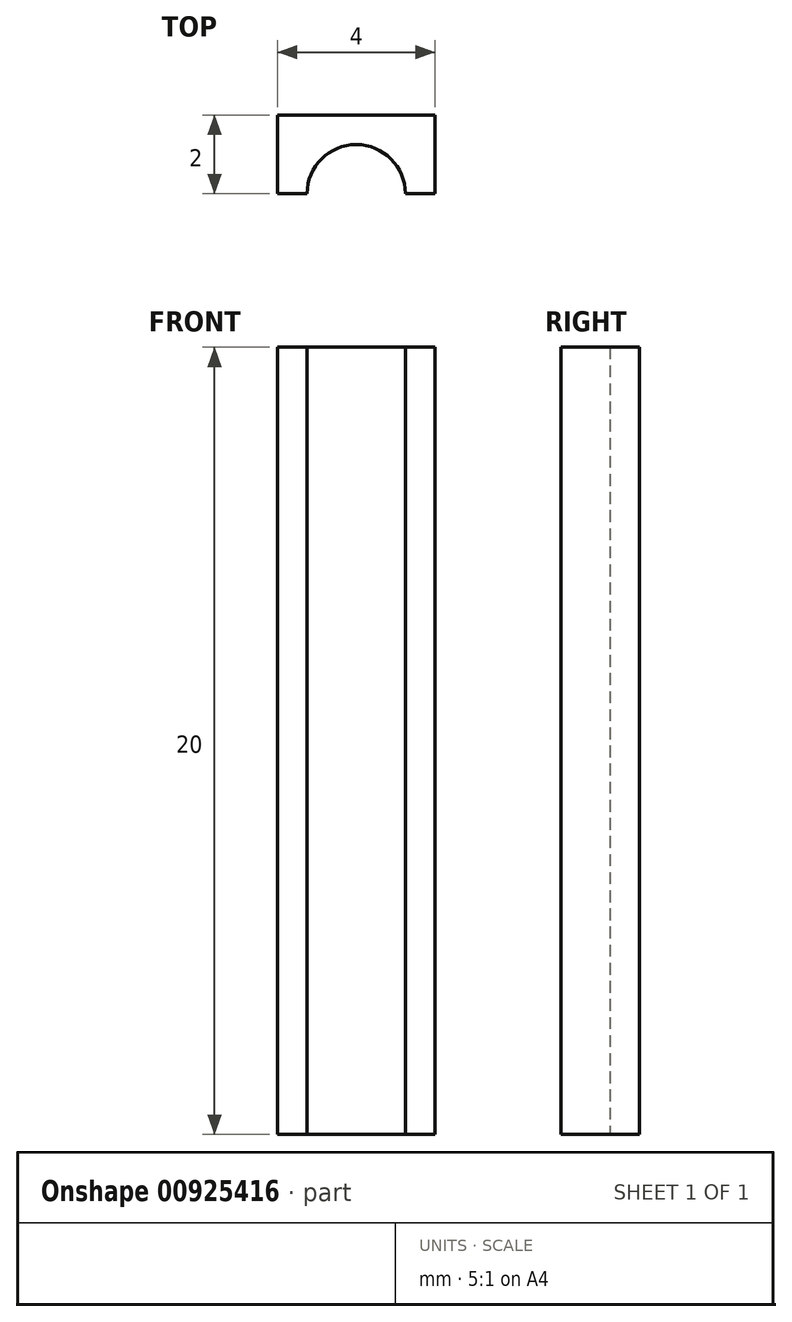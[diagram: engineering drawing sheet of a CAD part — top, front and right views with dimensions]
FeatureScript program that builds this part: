
annotation { "Feature Type Name" : "Feature", "Feature Type Description" : "" }
export const myFeature = defineFeature(function(context is Context, id is Id, definition is map)
    precondition{}
    {
        {
            var Q0;
            Q0=qCreatedBy(makeId("Top.planeOp"),FACE);
            var sketch = newSketch(context, id + "F0", { "sketchPlane" : qUnion([Q0])});
            skLineSegment(sketch, "E0.bottom", {"start": v(2, -1) * mm, "end": v(1.25, -1) * mm});
            skLineSegment(sketch, "E0.top", {"start": v(2, 1) * mm, "end": v(-2, 1) * mm});
            skLineSegment(sketch, "E0.left", {"start": v(2, -1) * mm, "end": v(2, 1) * mm});
            skLineSegment(sketch, "E0.right", {"start": v(-2, -1) * mm, "end": v(-2, 1) * mm});
            skPoint(sketch, "E0.middle", {"position": v(0, 0) * mm});
            skArc(sketch, "E1", {"start": v(1.25, -1) * mm, "mid": v(0, 0.25) * mm, "end": v(-1.25, -1) * mm});
            skLineSegment(sketch, "E2.trimOffspring", {"start": v(-1.25, -1) * mm, "end": v(-2, -1) * mm});
            skSolve(sketch);
        }
        {
            var Q0;
            Q0=makeQuery(id+"F0.imprint","IMPRINT",FACE,{"disambiguationData":[TD([[makeQuery(id+"F0.imprint","IMPRINT",EDGE,{"derivedFrom":sQuery(id+"F0.wireOp",EDGE,"E0.bottom")}),-1.0]])]});
            extrude(context, id + "F1", {"entities" : qUnion([Q0]), "depth" : 20 * mm, "offsetDistance" : 25 * mm});
        }
    });
